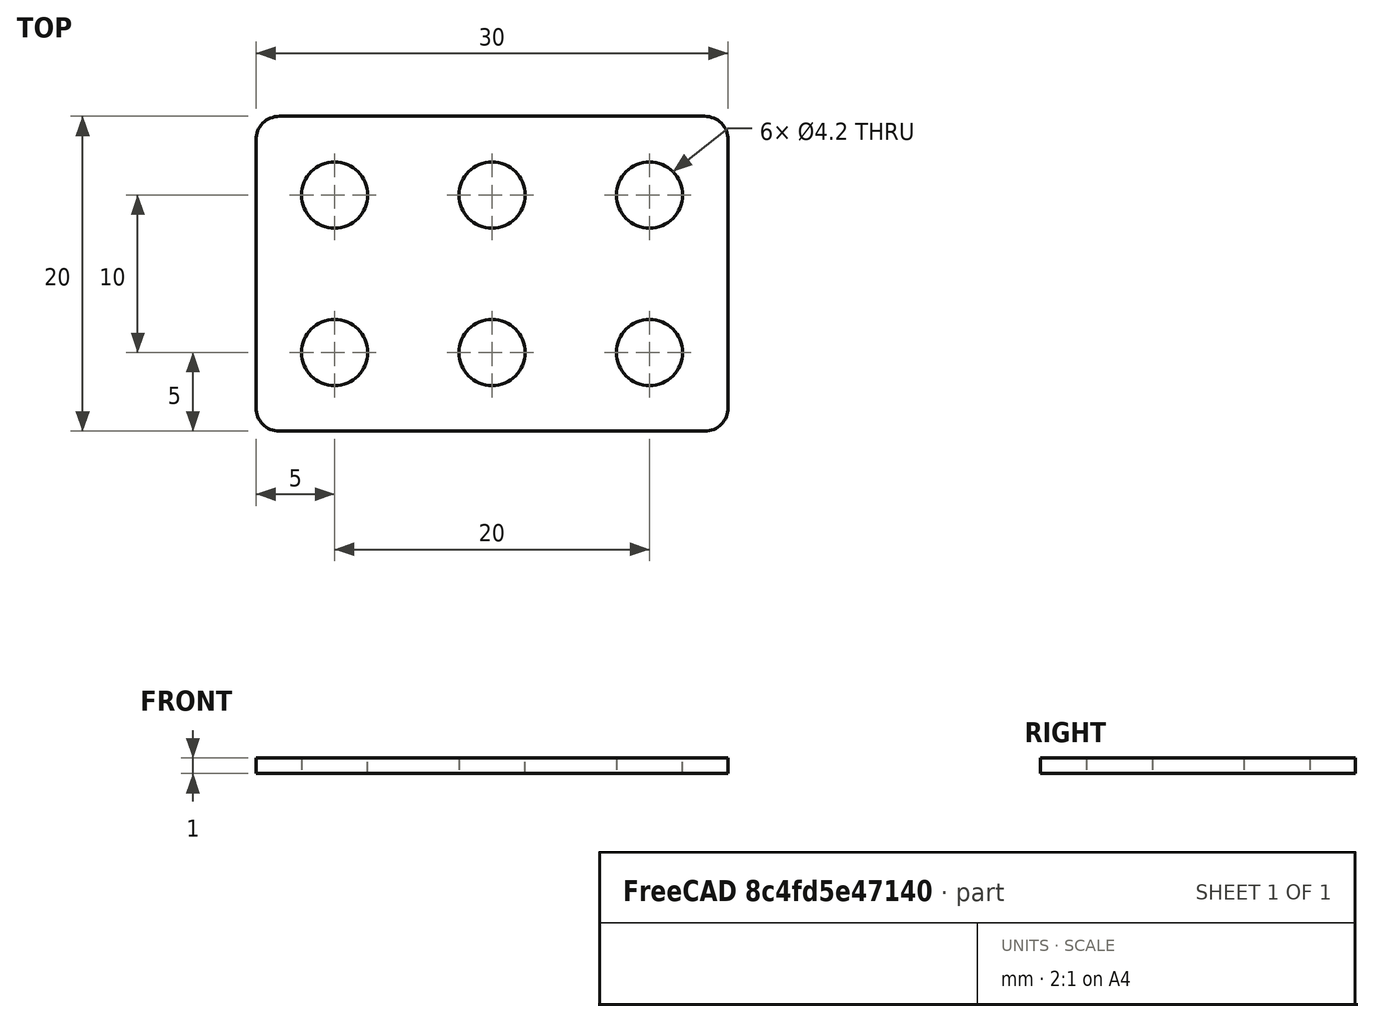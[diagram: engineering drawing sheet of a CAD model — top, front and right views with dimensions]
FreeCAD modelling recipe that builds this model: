
FCSTD DOCUMENT  (FreeCAD 0.16RUnknown)
Label: strip_2x3
License: All rights reserved
LicenseURL: http://en.wikipedia.org/wiki/All_rights_reserved
objects: Sketcher::SketchObject×1, PartDesign::Pad×1
note: 3 computed .brp shape members not serialized (recipe doc carries the construction recipe); baked Part::Feature solids carry a one-line shape summary decoded from their .brp

FEATURE [Sketcher::SketchObject] Sketch
  sketch-geometry (18):
    g0: LineSegment StartX=-3.5 StartY=15 StartZ=0 EndX=23.5 EndY=15 EndZ=0
    g1: LineSegment StartX=25 StartY=13.5 StartZ=0 EndX=25 EndY=-3.5 EndZ=0
    g2: LineSegment StartX=23.5 StartY=-5 StartZ=0 EndX=-3.5 EndY=-5 EndZ=0
    g3: LineSegment StartX=-5 StartY=-3.5 StartZ=0 EndX=-5 EndY=13.5 EndZ=0
    g4: ArcOfCircle CenterX=23.5 CenterY=13.5 CenterZ=0 NormalX=0 NormalY=0 NormalZ=1 Radius=1.5 StartAngle=0 EndAngle=1.5708
    g5: ArcOfCircle CenterX=23.5 CenterY=-3.5 CenterZ=0 NormalX=0 NormalY=0 NormalZ=1 Radius=1.5 StartAngle=4.71239 EndAngle=6.28319
    g6: ArcOfCircle CenterX=-3.5 CenterY=-3.5 CenterZ=0 NormalX=0 NormalY=0 NormalZ=1 Radius=1.5 StartAngle=3.14159 EndAngle=4.71239
    g7: ArcOfCircle CenterX=-3.5 CenterY=13.5 CenterZ=0 NormalX=0 NormalY=0 NormalZ=1 Radius=1.5 StartAngle=1.5708 EndAngle=3.14159
    g8: Circle CenterX=0 CenterY=0 CenterZ=0 NormalX=0 NormalY=0 NormalZ=1 Radius=2.1
    g9: Circle CenterX=0 CenterY=10 CenterZ=0 NormalX=0 NormalY=0 NormalZ=1 Radius=2.1
    g10: Circle CenterX=10 CenterY=0 CenterZ=0 NormalX=0 NormalY=0 NormalZ=1 Radius=2.1
    g11: LineSegment [constr] StartX=0 StartY=0 StartZ=0 EndX=10 EndY=0 EndZ=0
    g12: Circle CenterX=20 CenterY=0 CenterZ=0 NormalX=0 NormalY=0 NormalZ=1 Radius=2.1
    g13: LineSegment [constr] StartX=10 StartY=0 StartZ=0 EndX=20 EndY=0 EndZ=0
    g14: Circle CenterX=10 CenterY=10 CenterZ=0 NormalX=0 NormalY=0 NormalZ=1 Radius=2.1
    g15: LineSegment [constr] StartX=0 StartY=10 StartZ=0 EndX=10 EndY=10 EndZ=0
    g16: Circle CenterX=20 CenterY=10 CenterZ=0 NormalX=0 NormalY=0 NormalZ=1 Radius=2.1
    g17: LineSegment [constr] StartX=10 StartY=10 StartZ=0 EndX=20 EndY=10 EndZ=0
  constraints (45):
    c: Horizontal(g0)
    c: Horizontal(g2)
    c: Vertical(g1)
    c: Vertical(g3)
    c: Tangent(g0,g4) = 1.5708
    c: Tangent(g1,g4) = 1.5708
    c: Tangent(g1,g5) = 1.5708
    c: Tangent(g2,g5) = 1.5708
    c: Tangent(g3,g6) = 1.5708
    c: Tangent(g2,g6) = 1.5708
    c: Tangent(g3,g7) = 1.5708
    c: Tangent(g0,g7) = 1.5708
    c: Radius(g7) = 1.5
    c: Equal(g7,g4)
    c: Equal(g7,g5)
    c: Equal(g7,g6)
    c: Coincident(g8,g-1)
    c: Radius(g8) = 2.1
    c: Equal(g8,g9)
    c: DistanceY(g-1,g9) = 10
    c: DistanceX(g-1,g9) = 0
    c: Equal(g8,g10) = 2.1
    c: Coincident(g8,g11)
    c: Coincident(g10,g11)
    c: Distance(g11) = 10
    c: Angle(g11) = 0
    c: Equal(g8,g12) = 2.1
    c: Coincident(g10,g13)
    c: Coincident(g12,g13)
    c: Equal(g11,g13)
    c: Parallel(g13,g11)
    c: Coincident(g9,g15)
    c: Coincident(g14,g15)
    c: Distance(g15) = 10
    c: Angle(g15) = 0
    c: Coincident(g14,g17)
    c: Coincident(g16,g17)
    c: Equal(g15,g17)
    c: Parallel(g17,g15)
    c: Equal(g8,g14)
    c: Equal(g8,g16)
    c: DistanceX(g3,g9) = 5
    c: DistanceY(g9,g0) = 5
    c: DistanceY(g2,g12) = 5
    c: DistanceX(g12,g1) = 5
FEATURE [PartDesign::Pad] Pad
  Length = 1
  Length2 = 100
  Sketch = -> Sketch
  Type = 0
